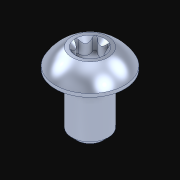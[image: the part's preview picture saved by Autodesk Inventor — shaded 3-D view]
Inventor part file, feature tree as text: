
AUTODESK INVENTOR PART (.ipt)
format: ipt  version: 2021 (Build 250183000, 183)  size: 280,064 bytes
history: native  units: in
note: dims shown in document units (in); Inventor stores cm internally (conversion verified against a paired STEP export)
features: other x32, sketch x5, extrude x1, thread x1, projected_geometry x1
ambient origin geometry x8: Origin, YZ Plane, XZ Plane, XY Plane, X Axis, Y Axis, Z Axis, Center Point
bodies: Solid1 (feature_tree), Body (feature_tree)
feature tree (40):
  other  "Table"
  other  "SScrew Star Smooth .250"
  other  "SScrew Star Smooth .290"
  other  "SScrew Star Smooth .375"
  other  "SScrew Star Smooth .500"
  other  "SScrew Star Smooth .625"
  other  "SScrew Star Smooth .750"
  other  "SScrew Star Smooth .875"
  other  "SScrew Star Smooth 1.000"
  other  "SScrew Star Smooth 1.250"
  other  "SScrew Star Smooth 1.500"
  other  "SScrew Star Smooth 1.750"
  other  "SScrew Star Smooth 2.000"
  other  "SScrew Star Smooth 2.250"
  other  "SScrew Star Smooth 2.500"
  other  "SScrew Star Threaded .250"
  other  "SScrew Star Threaded .290"
  other  "SScrew Star Threaded .375"
  other  "SScrew Star Threaded .500"
  other  "SScrew Star Threaded .625"
  other  "SScrew Star Threaded .750"
  other  "SScrew Star Threaded .875"
  other  "SScrew Star Threaded 1.000"
  other  "SScrew Star Threaded 1.250"
  other  "SScrew Star Threaded 1.500"
  other  "SScrew Star Threaded 1.750"
  other  "SScrew Star Threaded 2.000"
  other  "SScrew Star Threaded 2.250"
  other  "SScrew Star Threaded 2.500"
  other  "Head"
  extrude  "Hex"  Depth=0.164in
  other  "Head Chamfer"
  thread  "Thread"  [1 undecoded]
  other  "Tapered End"
  sketch  "Sketch1"  dims[d1=0.0in d4=0.164in d5=0.156in]
  sketch  "Sketch2"  dims[d6=0.015in]
  sketch  "Sketch4"  dims[d13=0.004in]
  sketch  "Sketch5"  dims[d14=0.082in]
  sketch  "Sketch6"  dims[d15=0.087in d16=0.0in d17=0.066in d20=90.0deg d22=0.07in d23=0.0in d29=0.066in d30=90.0deg d31=30.0deg d32=60.0deg d37=0.031in d38=0.275in d39=11.811in d40=0.0in d41=90.0deg d42=90.0deg d43=0.0in d44=0.0in d46=0.0312in d49=0.0585in d50=135.0deg d53=90.0deg d54=0.0027in d55=0.0205in d56=0.0039in d57=0.1378in d58=0.115in d59=0.163in d60=1.1811in d62=120.0deg]
  projected_geometry  "Projected Loop1"
note: 1 required parameter value undecoded (feature->parameter linkage not recoverable at this tier; creation-order binding heuristic only, values carry confidence <= 0.55)
